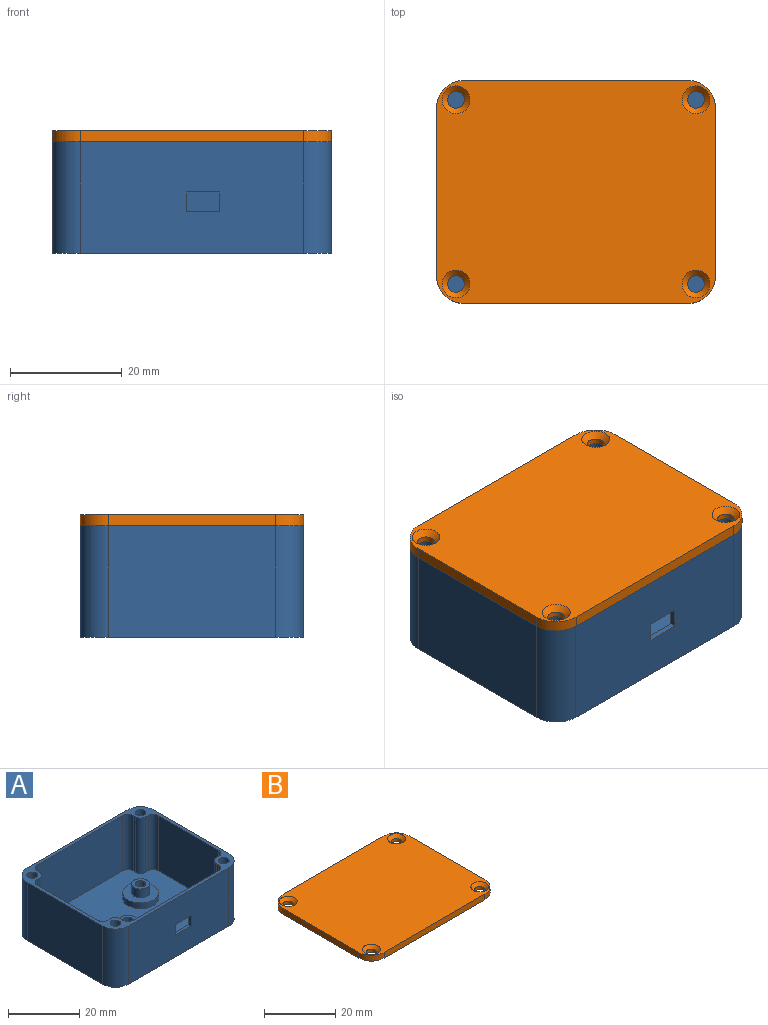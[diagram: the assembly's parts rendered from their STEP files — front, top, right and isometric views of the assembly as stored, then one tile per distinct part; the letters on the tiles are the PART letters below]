
ASSEMBLY  parts=2 mates=1
PART A: 71 faces, bbox 50x40x20 mm
  f0: plane 34x19mm, normal (0,1,0), area 625mm2, adj f5,f9,f55,f59,f67,f68,f69,f70
  f1: plane 40x20mm, normal (0,-1,0), area 779mm2, adj f2,f9,f52,f53,f67,f68,f69,f70
  f2: plane 50x40mm, normal (0,0,-1), area 1931.8mm2, adj f1,f10,f11,f12,f37,f38,f39,f40
  f3: cylinder r=1.5mm len=4mm, axis (0,0,-1), area 37.7mm2, adj f30,f50
  f4: cylinder r=1.5mm len=4mm, axis (0,0,-1), area 37.7mm2, adj f32,f43
  f5: plane 48x38mm, normal (0,0,1), area 1563.5mm2, adj f0,f6,f7,f8,f13,f14,f15,f16
  f6: plane 24x19mm, normal (-1,0,0), area 456mm2, adj f5,f9,f57,f61
  f7: plane 24x19mm, normal (1,0,0), area 456mm2, adj f5,f9,f60,f66
  f8: plane 34x19mm, normal (0,-1,0), area 646mm2, adj f5,f9,f62,f64
  f9: plane 50x40mm, normal (0,0,1), area 229.7mm2, adj f0,f1,f6,f7,f8,f10,f11,f12
  f10: plane 40x20mm, normal (0,1,0), area 800mm2, adj f2,f9,f51,f54
  f11: plane 30x20mm, normal (-1,0,0), area 600mm2, adj f2,f9,f51,f52
  f12: plane 30x20mm, normal (1,0,0), area 600mm2, adj f2,f9,f53,f54
  f13: plane 19x1mm, normal (0,-1,0), area 19mm2, adj f5,f9,f65,f66
  f14: plane 19x1mm, normal (1,0,0), area 19mm2, adj f5,f9,f64,f65
  f15: plane 19x1mm, normal (0,-1,0), area 19mm2, adj f5,f9,f61,f63
  f16: plane 19x1mm, normal (-1,0,0), area 19mm2, adj f5,f9,f62,f63
  f17: plane 19x1mm, normal (0,1,0), area 19mm2, adj f5,f9,f58,f60
  f18: plane 19x1mm, normal (1,0,0), area 19mm2, adj f5,f9,f58,f59
  f19: plane 19x1mm, normal (0,1,0), area 19mm2, adj f5,f9,f56,f57
  f20: plane 19x1mm, normal (-1,0,0), area 19mm2, adj f5,f9,f55,f56
  f21: cylinder r=1.5mm len=10mm, axis (0,0,1), area 94.2mm2, adj f9,f22
  f22: plane 3x3mm, normal (0,0,1), area 7.1mm2, adj f21
  f23: cylinder r=1.5mm len=10mm, axis (0,0,1), area 94.2mm2, adj f9,f24
  f24: plane 3x3mm, normal (0,0,1), area 7.1mm2, adj f23
  f25: cylinder r=1.5mm len=10mm, axis (0,0,1), area 94.2mm2, adj f9,f26
  f26: plane 3x3mm, normal (0,0,1), area 7.1mm2, adj f25
  f27: cylinder r=1.5mm len=10mm, axis (0,0,1), area 94.2mm2, adj f9,f28
  f28: plane 3x3mm, normal (0,0,1), area 7.1mm2, adj f27
  f29: cylinder r=2.5mm len=5mm, axis (0,0,-1), area 47.1mm2, adj f30,f34
  f30: plane 5x5mm, normal (0,0,1), area 12.6mm2, adj f3,f29
  f31: cylinder r=2.5mm len=5mm, axis (0,0,-1), area 47.1mm2, adj f32,f36
  f32: plane 5x5mm, normal (0,0,1), area 12.6mm2, adj f4,f31
  f33: cylinder r=5mm len=10mm, axis (0,0,-1), area 62.8mm2, adj f5,f34
  f34: plane 10x10mm, normal (0,0,1), area 58.9mm2, adj f29,f33
  f35: cylinder r=5mm len=10mm, axis (0,0,-1), area 62.8mm2, adj f5,f36
  f36: plane 10x10mm, normal (0,0,1), area 58.9mm2, adj f31,f35
  f37: plane 2.6x2mm, normal (-0.5,-0.87,0), area 6mm2, adj f2,f38,f42,f43
  f38: plane 3x2mm, normal (-1,0,0), area 6mm2, adj f2,f37,f39,f43
  f39: plane 2.6x2mm, normal (-0.5,0.87,0), area 6mm2, adj f2,f38,f40,f43
  f40: plane 2.6x2mm, normal (0.5,0.87,0), area 6mm2, adj f2,f39,f41,f43
  f41: plane 3x2mm, normal (1,0,0), area 6mm2, adj f2,f40,f42,f43
  f42: plane 2.6x2mm, normal (0.5,-0.87,0), area 6mm2, adj f2,f37,f41,f43
  f43: plane 6x5.2mm, normal (0,0,-1), area 16.3mm2, adj f4,f37,f38,f39,f40,f41,f42
  f44: plane 2.6x2mm, normal (-0.5,-0.87,0), area 6mm2, adj f2,f45,f49,f50
  f45: plane 3x2mm, normal (-1,0,0), area 6mm2, adj f2,f44,f46,f50
  f46: plane 2.6x2mm, normal (-0.5,0.87,0), area 6mm2, adj f2,f45,f47,f50
  f47: plane 2.6x2mm, normal (0.5,0.87,0), area 6mm2, adj f2,f46,f48,f50
  f48: plane 3x2mm, normal (1,0,0), area 6mm2, adj f2,f47,f49,f50
  f49: plane 2.6x2mm, normal (0.5,-0.87,0), area 6mm2, adj f2,f44,f48,f50
  f50: plane 6x5.2mm, normal (0,0,-1), area 16.3mm2, adj f3,f44,f45,f46,f47,f48,f49
  f51: cylinder r=5mm len=20mm, axis (0,0,1), area 157.1mm2, adj f2,f9,f10,f11
  f52: cylinder r=5mm len=20mm, axis (0,0,-1), area 157.1mm2, adj f1,f2,f9,f11
  f53: cylinder r=5mm len=20mm, axis (0,0,1), area 157.1mm2, adj f1,f2,f9,f12
  f54: cylinder r=5mm len=20mm, axis (0,0,-1), area 157.1mm2, adj f2,f9,f10,f12
  f55: cylinder r=2mm len=19mm, axis (0,0,1), area 59.7mm2, adj f0,f5,f9,f20
  f56: cylinder r=2mm len=19mm, axis (0,0,1), area 59.7mm2, adj f5,f9,f19,f20
  f57: cylinder r=2mm len=19mm, axis (0,0,1), area 59.7mm2, adj f5,f6,f9,f19
  f58: cylinder r=2mm len=19mm, axis (0,0,1), area 59.7mm2, adj f5,f9,f17,f18
  f59: cylinder r=2mm len=19mm, axis (0,0,-1), area 59.7mm2, adj f0,f5,f9,f18
  f60: cylinder r=2mm len=19mm, axis (0,0,1), area 59.7mm2, adj f5,f7,f9,f17
  f61: cylinder r=2mm len=19mm, axis (0,0,-1), area 59.7mm2, adj f5,f6,f9,f15
  f62: cylinder r=2mm len=19mm, axis (0,0,1), area 59.7mm2, adj f5,f8,f9,f16
  f63: cylinder r=2mm len=19mm, axis (0,0,1), area 59.7mm2, adj f5,f9,f15,f16
  f64: cylinder r=2mm len=19mm, axis (0,0,-1), area 59.7mm2, adj f5,f8,f9,f14
  f65: cylinder r=2mm len=19mm, axis (0,0,1), area 59.7mm2, adj f5,f9,f13,f14
  f66: cylinder r=2mm len=19mm, axis (0,0,-1), area 59.7mm2, adj f5,f7,f9,f13
  f67: plane 6x1mm, normal (0,0,-1), area 6mm2, adj f0,f1,f68,f70
  f68: plane 3.5x1mm, normal (1,0,0), area 3.5mm2, adj f0,f1,f67,f69
  f69: plane 6x1mm, normal (0,0,1), area 6mm2, adj f0,f1,f68,f70
  f70: plane 3.5x1mm, normal (-1,0,0), area 3.5mm2, adj f0,f1,f67,f69
PART B: 18 faces, bbox 50x40x2 mm
  f0: plane 30x2mm, normal (-1,0,0), area 60mm2, adj f4,f5,f14,f17
  f1: plane 40x2mm, normal (0,-1,0), area 80mm2, adj f4,f5,f14,f15
  f2: plane 30x2mm, normal (1,0,0), area 60mm2, adj f4,f5,f15,f16
  f3: plane 40x2mm, normal (0,1,0), area 80mm2, adj f4,f5,f16,f17
  f4: plane 50x40mm, normal (0,0,1), area 1900mm2, adj f0,f1,f2,f3,f10,f11,f12,f13
  f5: plane 50x40mm, normal (0,0,-1), area 1950.3mm2, adj f0,f1,f2,f3,f6,f7,f8,f9
  f6: cylinder r=1.5mm len=3mm, axis (0,0,1), area 9.4mm2, adj f5,f10
  f7: cylinder r=1.5mm len=3mm, axis (0,0,1), area 9.4mm2, adj f5,f13
  f8: cylinder r=1.5mm len=3mm, axis (0,0,1), area 9.4mm2, adj f5,f12
  f9: cylinder r=1.5mm len=3mm, axis (0,0,1), area 9.4mm2, adj f5,f11
  f10: cone r=1.5mm half-angle=45deg, axis (0,0,1), area 17.8mm2, adj f4,f6
  f11: cone r=1.5mm half-angle=45deg, axis (0,0,1), area 17.8mm2, adj f4,f9
  f12: cone r=1.5mm half-angle=45deg, axis (0,0,1), area 17.8mm2, adj f4,f8
  f13: cone r=1.5mm half-angle=45deg, axis (0,0,1), area 17.8mm2, adj f4,f7
  f14: cylinder r=5mm len=5mm, axis (0,0,1), area 15.7mm2, adj f0,f1,f4,f5
  f15: cylinder r=5mm len=5mm, axis (0,0,-1), area 15.7mm2, adj f1,f2,f4,f5
  f16: cylinder r=5mm len=5mm, axis (0,0,1), area 15.7mm2, adj f2,f3,f4,f5
  f17: cylinder r=5mm len=5mm, axis (0,0,-1), area 15.7mm2, adj f0,f3,f4,f5
PLACE A t=(-72.15,-40.42,25.63)mm fixed
PLACE B t=(-144.6,-46.96,45.63)mm
MATE slider A.f25 <-> B.f9  axis (0,0,1) through (-84.86,-24.86,45.63)mm
